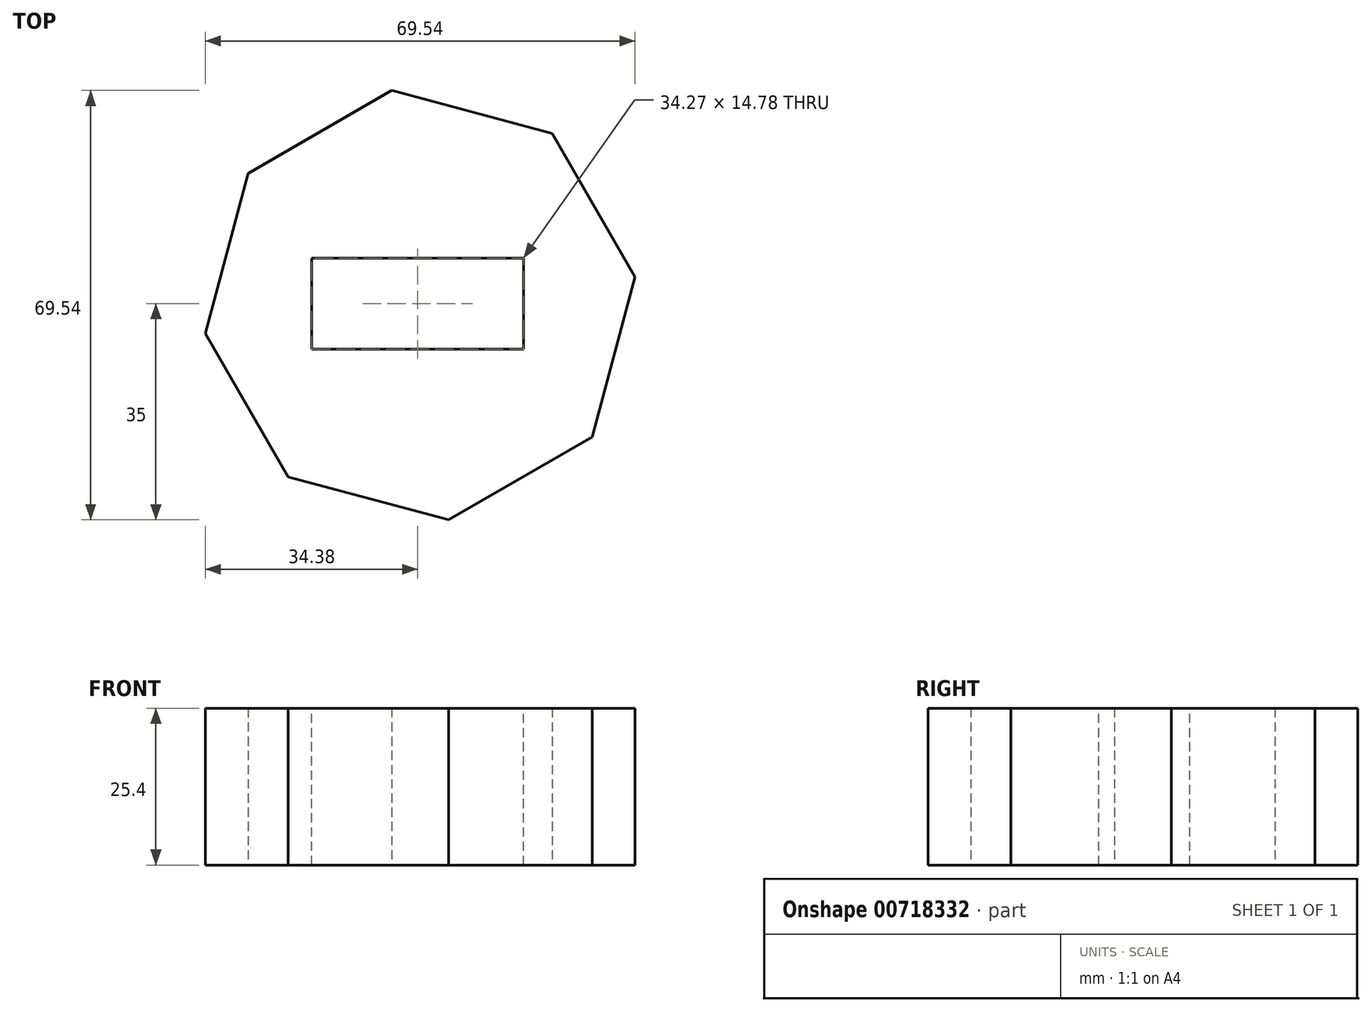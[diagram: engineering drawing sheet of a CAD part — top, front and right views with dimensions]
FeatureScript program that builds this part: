
annotation { "Feature Type Name" : "Feature", "Feature Type Description" : "" }
export const myFeature = defineFeature(function(context is Context, id is Id, definition is map)
    precondition{}
    {
        {
            var Q0;
            Q0=qCreatedBy(makeId("Top.planeOp"),FACE);
            var sketch = newSketch(context, id + "F0", { "sketchPlane" : qUnion([Q0])});
            skCircle(sketch, "E0.cCircle", {"center": v(0, 0) * mm, "radius": 32.4 * mm, "construction": true});
            skLineSegment(sketch, "E0.0", {"start": v(21.35, 27.83) * mm, "end": v(34.77, 4.58) * mm});
            skLineSegment(sketch, "E0.1", {"start": v(34.77, 4.58) * mm, "end": v(27.83, -21.35) * mm});
            skLineSegment(sketch, "E0.2", {"start": v(27.83, -21.35) * mm, "end": v(4.58, -34.77) * mm});
            skLineSegment(sketch, "E0.3", {"start": v(4.58, -34.77) * mm, "end": v(-21.35, -27.83) * mm});
            skLineSegment(sketch, "E0.4", {"start": v(-21.35, -27.83) * mm, "end": v(-34.77, -4.58) * mm});
            skLineSegment(sketch, "E0.5", {"start": v(-34.77, -4.58) * mm, "end": v(-27.83, 21.35) * mm});
            skLineSegment(sketch, "E0.6", {"start": v(-27.83, 21.35) * mm, "end": v(-4.58, 34.77) * mm});
            skLineSegment(sketch, "E0.7", {"start": v(-4.58, 34.77) * mm, "end": v(21.35, 27.83) * mm});
            skPoint(sketch, "E0.0.midPoint", {"position": v(28.06, 16.2) * mm});
            skSolve(sketch);
        }
        {
            var Q0;
            Q0 = qSketchRegion(id + "F0", true);
            extrude(context, id + "F1", {"entities" : qUnion([Q0]), "depth" : 25.4 * mm, "offsetDistance" : 25.4 * mm});
        }
        {
            var Q0;
            Q0=makeQuery(id+"F1.opExtrude","CAP_FACE",FACE,{"disambiguationData":[OSD([sQuery(id+"F0.wireOp",EDGE,"E0.0"),sQuery(id+"F0.wireOp",EDGE,"E0.1"),sQuery(id+"F0.wireOp",EDGE,"E0.2"),sQuery(id+"F0.wireOp",EDGE,"E0.3"),sQuery(id+"F0.wireOp",EDGE,"E0.4"),sQuery(id+"F0.wireOp",EDGE,"E0.5"),sQuery(id+"F0.wireOp",EDGE,"E0.6"),sQuery(id+"F0.wireOp",EDGE,"E0.7")])],"isStart":false});
            var sketch = newSketch(context, id + "F2", { "sketchPlane" : qUnion([Q0])});
            skLineSegment(sketch, "E1.bottom", {"start": v(-17.53, 7.62) * mm, "end": v(16.75, 7.62) * mm});
            skLineSegment(sketch, "E1.top", {"start": v(-17.53, -7.16) * mm, "end": v(16.75, -7.16) * mm});
            skLineSegment(sketch, "E1.left", {"start": v(-17.53, 7.62) * mm, "end": v(-17.53, -7.16) * mm});
            skLineSegment(sketch, "E1.right", {"start": v(16.75, 7.62) * mm, "end": v(16.75, -7.16) * mm});
            skSolve(sketch);
        }
        {
            var Q0;
            Q0 = qSketchRegion(id + "F2", true);
            extrude(context, id + "F3", {"entities" : qUnion([Q0]), "operationType" : NewBodyOperationType.REMOVE, "oppositeDirection" : true, "depth" : 36.32 * mm, "offsetDistance" : 25.4 * mm});
        }
    });
